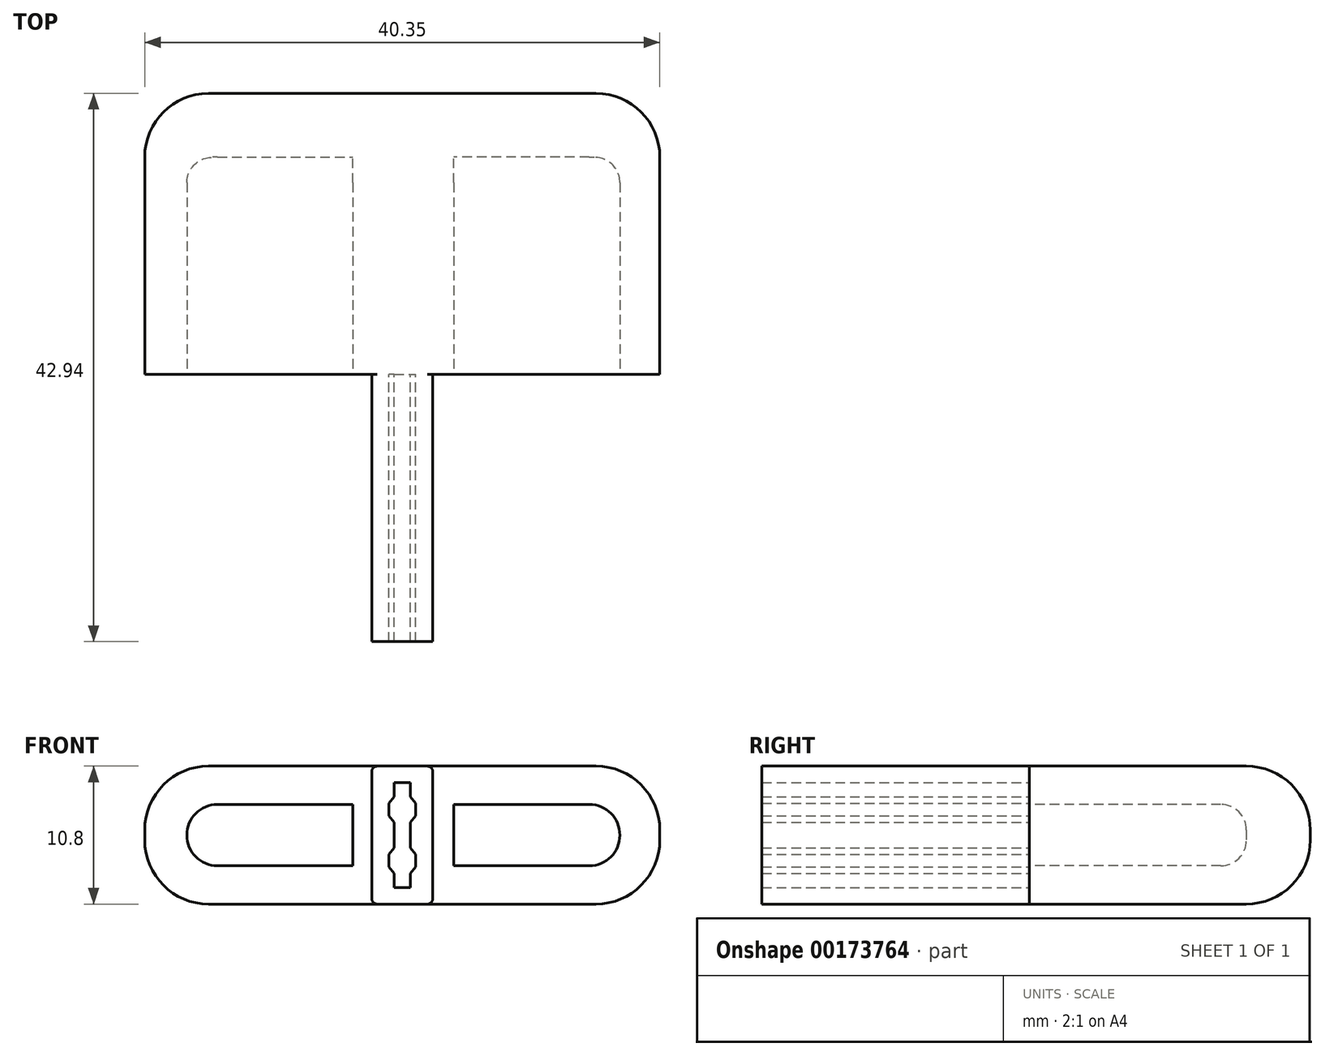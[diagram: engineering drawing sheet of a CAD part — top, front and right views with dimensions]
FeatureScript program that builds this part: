
annotation { "Feature Type Name" : "Feature", "Feature Type Description" : "" }
export const myFeature = defineFeature(function(context is Context, id is Id, definition is map)
    precondition{}
    {
        {
            var Q0;
            Q0=qCreatedBy(makeId("Front.planeOp"),FACE);
            var sketch = newSketch(context, id + "F0", { "sketchPlane" : qUnion([Q0])});
            skLineSegment(sketch, "E0.bottom", {"start": v(0.4, 0) * mm, "end": v(4.35, 0) * mm});
            skLineSegment(sketch, "E0.top", {"start": v(0.4, 10.8) * mm, "end": v(4.35, 10.8) * mm});
            skLineSegment(sketch, "E0.left", {"start": v(0, 0.4) * mm, "end": v(0, 10.4) * mm});
            skLineSegment(sketch, "E0.right", {"start": v(4.75, 0.4) * mm, "end": v(4.75, 10.4) * mm});
            skLineSegment(sketch, "E1.bottom", {"start": v(1.74, 9.53) * mm, "end": v(3, 9.53) * mm});
            skLineSegment(sketch, "E1.top", {"start": v(1.74, 1.28) * mm, "end": v(3, 1.28) * mm});
            skLineSegment(sketch, "E1.left", {"start": v(1.74, 9.53) * mm, "end": v(1.74, 8.4) * mm});
            skLineSegment(sketch, "E1.right", {"start": v(3, 9.53) * mm, "end": v(3, 8.4) * mm});
            skLineSegment(sketch, "E2", {"start": v(2.37, 0) * mm, "end": v(2.37, 10.8) * mm, "construction": true});
            skLineSegment(sketch, "E3", {"start": v(1.34, 7.9) * mm, "end": v(1.34, 6.9) * mm});
            skLineSegment(sketch, "E4", {"start": v(1.74, 8.4) * mm, "end": v(1.34, 7.9) * mm});
            skLineSegment(sketch, "E5", {"start": v(1.34, 6.9) * mm, "end": v(1.74, 6.4) * mm});
            skLineSegment(sketch, "E6", {"start": v(0, 5.4) * mm, "end": v(4.75, 5.4) * mm, "construction": true});
            skLineSegment(sketch, "E7.trimOffspring", {"start": v(1.74, 6.4) * mm, "end": v(1.74, 4.4) * mm});
            skLineSegment(sketch, "E8.MirrorCS", {"start": v(1.34, 3.9) * mm, "end": v(1.74, 4.4) * mm});
            skLineSegment(sketch, "E9.MirrorCS", {"start": v(1.34, 2.9) * mm, "end": v(1.34, 3.9) * mm});
            skLineSegment(sketch, "E10.MirrorCS", {"start": v(1.74, 2.4) * mm, "end": v(1.34, 2.9) * mm});
            skLineSegment(sketch, "E11.trimOffspring", {"start": v(1.74, 2.4) * mm, "end": v(1.74, 1.28) * mm});
            skLineSegment(sketch, "E12.MirrorCS", {"start": v(3.01, 8.4) * mm, "end": v(3.4, 7.9) * mm});
            skLineSegment(sketch, "E13.MirrorCS", {"start": v(3.4, 7.9) * mm, "end": v(3.4, 6.9) * mm});
            skLineSegment(sketch, "E14.MirrorCS", {"start": v(3.4, 6.9) * mm, "end": v(3, 6.4) * mm});
            skLineSegment(sketch, "E15.MirrorCS", {"start": v(3.4, 3.9) * mm, "end": v(3, 4.4) * mm});
            skLineSegment(sketch, "E16.MirrorCS", {"start": v(3.4, 2.9) * mm, "end": v(3.4, 3.9) * mm});
            skLineSegment(sketch, "E17.MirrorCS", {"start": v(3.01, 2.4) * mm, "end": v(3.4, 2.9) * mm});
            skLineSegment(sketch, "E18.trimOffspring", {"start": v(3, 6.4) * mm, "end": v(3, 4.4) * mm});
            skLineSegment(sketch, "E19.trimOffspring", {"start": v(3, 2.4) * mm, "end": v(3, 1.28) * mm});
            skPoint(sketch, "E20.visualSharp", {"position": v(0, 10.8) * mm});
            skArc(sketch, "E20.filletArc", {"start": v(0.4, 10.8) * mm, "mid": v(0.12, 10.68) * mm, "end": v(0, 10.4) * mm});
            skPoint(sketch, "E21.visualSharp", {"position": v(4.75, 10.8) * mm});
            skArc(sketch, "E21.filletArc", {"start": v(4.75, 10.4) * mm, "mid": v(4.63, 10.68) * mm, "end": v(4.35, 10.8) * mm});
            skPoint(sketch, "E22.visualSharp", {"position": v(4.75, 0) * mm});
            skArc(sketch, "E22.filletArc", {"start": v(4.35, 0) * mm, "mid": v(4.63, 0.12) * mm, "end": v(4.75, 0.4) * mm});
            skPoint(sketch, "E23.visualSharp", {"position": v(0, 0) * mm});
            skArc(sketch, "E23.filletArc", {"start": v(0, 0.4) * mm, "mid": v(0.12, 0.12) * mm, "end": v(0.4, 0) * mm});
            skSolve(sketch);
        }
        {
            var Q0;
            Q0=makeQuery(id+"F0.imprint","IMPRINT",FACE,{"disambiguationData":[TD([[makeQuery(id+"F0.imprint","IMPRINT",EDGE,{"derivedFrom":sQuery(id+"F0.wireOp",EDGE,"E0.bottom")}),1.0]])]});
            extrude(context, id + "F1", {"entities" : qUnion([Q0]), "depth" : 20.94 * mm});
        }
        {
            var Q0;
            Q0=qCreatedBy(makeId("Front.planeOp"),FACE);
            var sketch = newSketch(context, id + "F2", { "sketchPlane" : qUnion([Q0])});
            skLineSegment(sketch, "E24.bottom", {"start": v(-17.8, 0) * mm, "end": v(22.55, 0) * mm});
            skLineSegment(sketch, "E24.top", {"start": v(-17.8, 10.8) * mm, "end": v(22.55, 10.8) * mm});
            skLineSegment(sketch, "E24.left", {"start": v(-17.8, 0) * mm, "end": v(-17.8, 10.8) * mm});
            skLineSegment(sketch, "E24.right", {"start": v(22.55, 0) * mm, "end": v(22.55, 10.8) * mm});
            skSolve(sketch);
        }
        {
            var Q0;
            Q0=makeQuery(id+"F2.imprint","IMPRINT",FACE,{"disambiguationData":[TD([[makeQuery(id+"F2.imprint","IMPRINT",EDGE,{"derivedFrom":sQuery(id+"F2.wireOp",EDGE,"E24.bottom")}),1.0]])]});
            extrude(context, id + "F3", {"entities" : qUnion([Q0]), "operationType" : NewBodyOperationType.ADD, "oppositeDirection" : true, "depth" : 22 * mm});
        }
        {
            var Q0;
            Q0=makeQuery(id+"F3.opExtrude","SWEPT_EDGE",EDGE,{"disambiguationData":[OSD([sQuery(id+"F2.wireOp",EDGE,"E24.top"),sQuery(id+"F2.wireOp",EDGE,"E24.left")])]});
            var Q1;
            Q1=makeQuery(id+"F3.opExtrude","CAP_EDGE",EDGE,{"disambiguationData":[OSD([sQuery(id+"F2.wireOp",EDGE,"E24.top")])],"isStart":false});
            var Q2;
            Q2=makeQuery(id+"F3.opExtrude","SWEPT_EDGE",EDGE,{"disambiguationData":[OSD([sQuery(id+"F2.wireOp",EDGE,"E24.top"),sQuery(id+"F2.wireOp",EDGE,"E24.right")])]});
            var Q3;
            Q3=makeQuery(id+"F3.opExtrude","CAP_EDGE",EDGE,{"disambiguationData":[OSD([sQuery(id+"F2.wireOp",EDGE,"E24.right")])],"isStart":false});
            var Q4;
            Q4=makeQuery(id+"F3.opExtrude","CAP_EDGE",EDGE,{"disambiguationData":[OSD([sQuery(id+"F2.wireOp",EDGE,"E24.left")])],"isStart":false});
            var Q5;
            Q5=makeQuery(id+"F3.opExtrude","SWEPT_EDGE",EDGE,{"disambiguationData":[OSD([sQuery(id+"F2.wireOp",EDGE,"E24.bottom"),sQuery(id+"F2.wireOp",EDGE,"E24.left")])]});
            var Q6;
            Q6=makeQuery(id+"F3.opExtrude","CAP_EDGE",EDGE,{"disambiguationData":[OSD([sQuery(id+"F2.wireOp",EDGE,"E24.bottom")])],"isStart":false});
            var Q7;
            Q7=makeQuery(id+"F3.opExtrude","SWEPT_EDGE",EDGE,{"disambiguationData":[OSD([sQuery(id+"F2.wireOp",EDGE,"E24.bottom"),sQuery(id+"F2.wireOp",EDGE,"E24.right")])]});
            fillet(context, id + "F4", {"entities" : qUnion([Q0, Q1, Q2, Q3, Q4, Q5, Q6, Q7]), "radius" : 5 * mm, "tangentPropagation" : true, "allowEdgeOverflow" : false});
        }
        {
            var Q0;
            Q0=qCreatedBy(makeId("Front.planeOp"),FACE);
            var sketch = newSketch(context, id + "F5", { "sketchPlane" : qUnion([Q0])});
            skLineSegment(sketch, "E25.bottom", {"start": v(-12.1, 7.8) * mm, "end": v(-1.5, 7.8) * mm});
            skLineSegment(sketch, "E25.top", {"start": v(-12.1, 3) * mm, "end": v(-1.5, 3) * mm});
            skLineSegment(sketch, "E25.right", {"start": v(-1.5, 7.8) * mm, "end": v(-1.5, 3) * mm});
            skArc(sketch, "E26", {"start": v(-12.1, 7.8) * mm, "mid": v(-14.5, 5.4) * mm, "end": v(-12.1, 3) * mm});
            skLineSegment(sketch, "E27", {"start": v(2.46, 0) * mm, "end": v(2.46, 13.37) * mm, "construction": true});
            skLineSegment(sketch, "E28.MirrorCS", {"start": v(6.42, 7.8) * mm, "end": v(6.42, 3) * mm});
            skLineSegment(sketch, "E29.MirrorCS", {"start": v(17.02, 7.8) * mm, "end": v(6.42, 7.8) * mm});
            skLineSegment(sketch, "E30.MirrorCS", {"start": v(17.02, 3) * mm, "end": v(6.42, 3) * mm});
            skArc(sketch, "E31.MirrorCS", {"start": v(17.02, 7.8) * mm, "mid": v(19.42, 5.4) * mm, "end": v(17.02, 3) * mm});
            skSolve(sketch);
        }
        {
            var Q0;
            Q0 = qSketchRegion(id + "F5", true);
            extrude(context, id + "F6", {"entities" : qUnion([Q0]), "operationType" : NewBodyOperationType.REMOVE, "oppositeDirection" : true, "depth" : 17 * mm});
        }
        {
            var Q0;
            Q0=makeQuery(id+"F6.boolean.opBoolean","COPY",EDGE,{"derivedFrom":makeQuery(id+"F6.opExtrude","CAP_EDGE",EDGE,{"disambiguationData":[OSD([sQuery(id+"F5.wireOp",EDGE,"E30.MirrorCS")])],"isStart":false})});
            var Q1;
            Q1=makeQuery(id+"F6.boolean.opBoolean","COPY",EDGE,{"derivedFrom":makeQuery(id+"F6.opExtrude","CAP_EDGE",EDGE,{"disambiguationData":[OSD([sQuery(id+"F5.wireOp",EDGE,"E25.top")])],"isStart":false})});
            fillet(context, id + "F7", {"entities" : qUnion([Q0, Q1]), "radius" : 2 * mm, "tangentPropagation" : true, "allowEdgeOverflow" : false});
        }
    });
